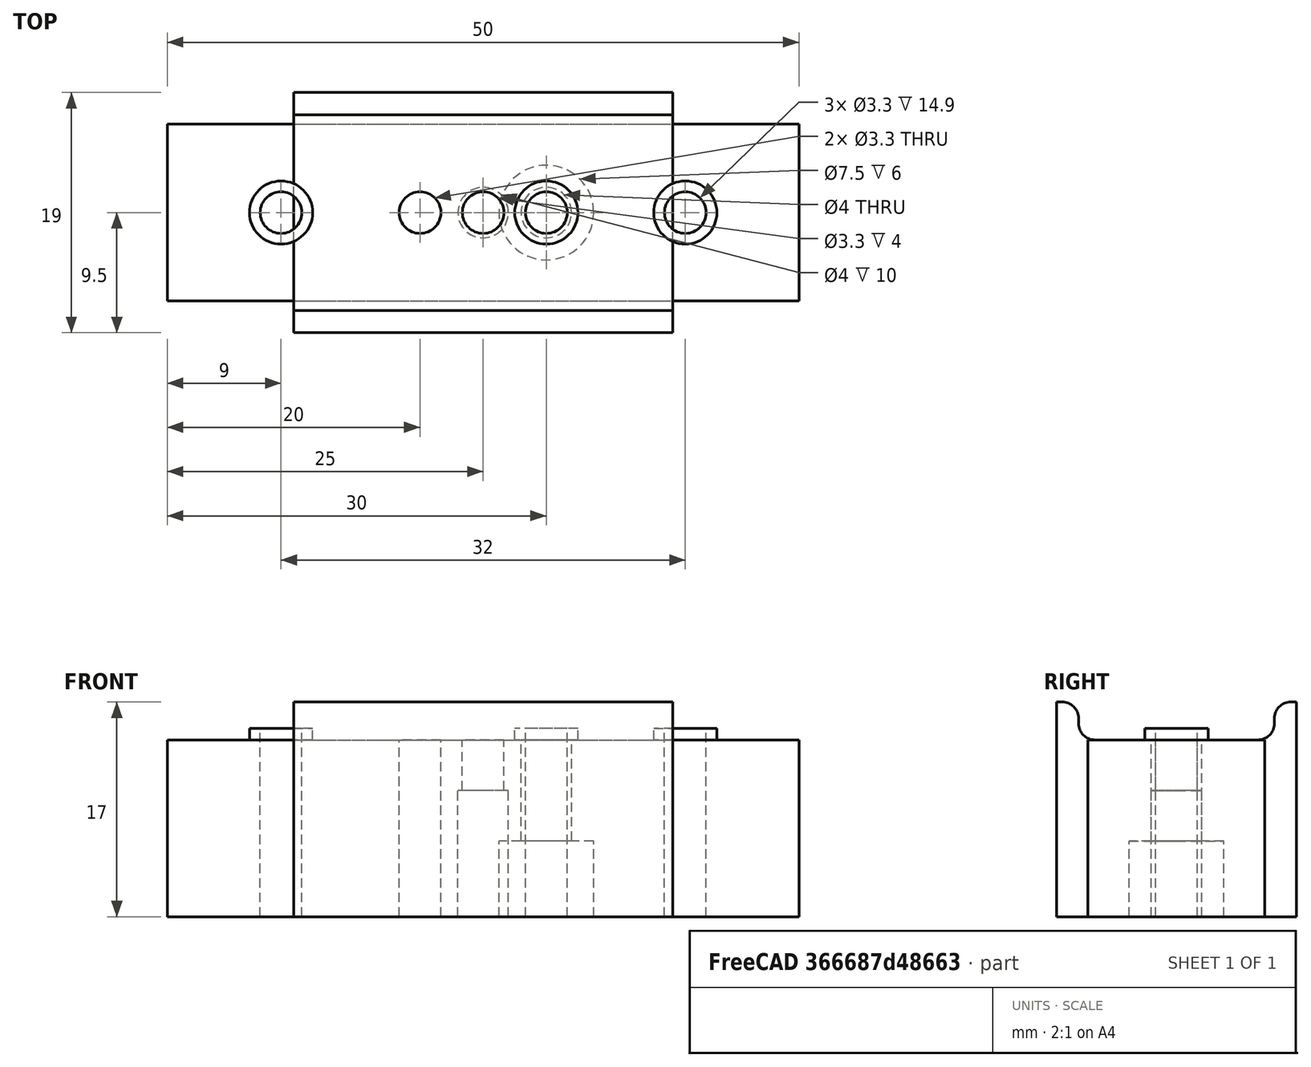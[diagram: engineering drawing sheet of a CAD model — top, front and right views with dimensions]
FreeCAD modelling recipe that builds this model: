
FCSTD DOCUMENT  (FreeCAD 0.15R4671 (Git))
Label: スライダ保持
License: All rights reserved
LicenseURL: http://en.wikipedia.org/wiki/All_rights_reserved
objects: Part::Cylinder×12, Part::Box×5, Part::MultiFuse×5, Part::Cut×5, Part::Fillet×2
note: 29 computed .brp shape members not serialized (recipe doc carries the construction recipe); baked Part::Feature solids carry a one-line shape summary decoded from their .brp

FEATURE [Part::Box] Box  label="立方体"
  Height = 14
  Length = 50
  Placement = pos=(-25,-7,0) rot=(0,0,1;0rad)
  Width = 14
FEATURE [Part::Cylinder] Cylinder  label="円柱"
  Angle = 360
  Height = 14.9
  Placement = pos=(16,0,0) rot=(0,0,1;0rad)
  Radius = 2.5
FEATURE [Part::Cylinder] Cylinder001  label="円柱001"
  Angle = 360
  Height = 14.9
  Placement = pos=(-16,0,0) rot=(0,0,1;0rad)
  Radius = 2.5
FEATURE [Part::Cylinder] Cylinder002  label="円柱002"
  Angle = 360
  Height = 14
  Radius = 1.65
FEATURE [Part::MultiFuse] Fusion
  Shapes = -> [Cylinder001,Cylinder,Box]
FEATURE [Part::Cylinder] Cylinder004  label="円柱004"
  Angle = 360
  Height = 10
  Radius = 2
FEATURE [Part::Cylinder] Cylinder005  label="円柱005"
  Angle = 360
  Height = 15
  Placement = pos=(16,0,0) rot=(0,0,1;0rad)
  Radius = 1.65
FEATURE [Part::Cylinder] Cylinder006  label="円柱006"
  Angle = 360
  Height = 15
  Placement = pos=(-16,0,0) rot=(0,0,1;0rad)
  Radius = 1.65
FEATURE [Part::Box] Box001  label="立方体001"
  Height = 17
  Length = 30
  Placement = pos=(-15,-9.5,0) rot=(0,0,1;0rad)
  Width = 19
FEATURE [Part::Box] Box002  label="立方体002"
  Height = 10
  Length = 30
  Placement = pos=(-15,-7.75,14) rot=(0,0,1;0rad)
  Width = 15.5
FEATURE [Part::Cut] Cut001
  Base = -> Box001
  Tool = -> Box002
FEATURE [Part::Fillet] Fillet
  Base = -> Cut001
  Edges = 4 edges r=1.3: [Edge9,Edge13,Edge14,Edge17]
FEATURE [Part::Box] Box003  label="立方体003"
  Height = 17
  Length = 30
  Placement = pos=(-15,-9.5,0) rot=(0,0,1;0rad)
  Width = 19
FEATURE [Part::Box] Box004  label="立方体004"
  Height = 10
  Length = 30
  Placement = pos=(-15,-7.75,14) rot=(0,0,1;0rad)
  Width = 15.5
FEATURE [Part::Cut] Cut002
  Base = -> Box003
  Tool = -> Box004
FEATURE [Part::Fillet] Fillet001
  Base = -> Cut002
  Edges = 4 edges r=1.3: [Edge9,Edge13,Edge14,Edge17]
FEATURE [Part::Cylinder] Cylinder007  label="円柱007"
  Angle = 360
  Height = 14.9
  Placement = pos=(5,0,0) rot=(0,0,1;0rad)
  Radius = 2.5
FEATURE [Part::Cylinder] Cylinder008  label="円柱008"
  Angle = 360
  Height = 14.9
  Placement = pos=(5,0,0) rot=(0,0,1;0rad)
  Radius = 1.65
FEATURE [Part::Cylinder] Cylinder009  label="円柱009"
  Angle = 360
  Height = 14
  Placement = pos=(-5,0,0) rot=(0,0,1;0rad)
  Radius = 1.65
FEATURE [Part::MultiFuse] Fusion002
  Shapes = -> [Cylinder007,Fillet]
FEATURE [Part::MultiFuse] Fusion004
  Shapes = -> [Cylinder002,Cylinder005,Cylinder006,Cylinder004]
FEATURE [Part::Cut] Cut
  Base = -> Fusion
  Tool = -> Fusion004
FEATURE [Part::MultiFuse] Fusion005
  Shapes = -> [Cylinder008,Cylinder009]
FEATURE [Part::Cut] Cut003
  Base = -> Fusion002
  Tool = -> Fusion005
FEATURE [Part::Cylinder] Cylinder010  label="円柱010"
  Angle = 360
  Height = 14
  Placement = pos=(5,0,0) rot=(0,0,1;0rad)
  Radius = 2
FEATURE [Part::Cylinder] Cylinder011  label="円柱011"
  Angle = 360
  Height = 6
  Placement = pos=(5,0,0) rot=(0,0,1;0rad)
  Radius = 3.75
FEATURE [Part::Cylinder] Cylinder012  label="円柱012"
  Angle = 360
  Height = 14
  Placement = pos=(-5,0,0) rot=(0,0,1;0rad)
  Radius = 1.65
FEATURE [Part::MultiFuse] Fusion006
  Shapes = -> [Cylinder010,Cylinder011,Cylinder012]
FEATURE [Part::Cut] Cut004
  Base = -> Fillet001
  Tool = -> Fusion006
